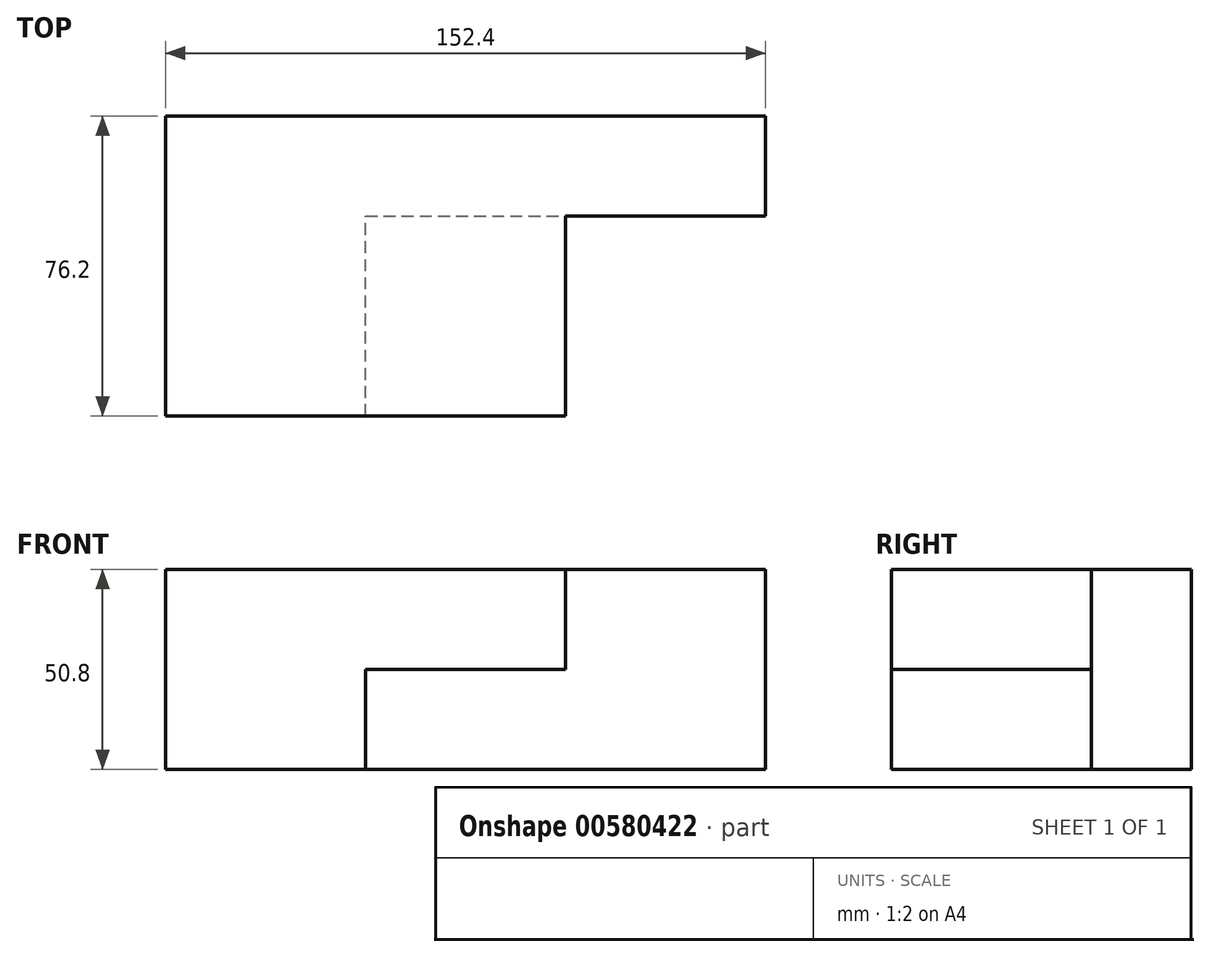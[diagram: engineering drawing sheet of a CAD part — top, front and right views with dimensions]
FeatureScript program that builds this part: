
annotation { "Feature Type Name" : "Feature", "Feature Type Description" : "" }
export const myFeature = defineFeature(function(context is Context, id is Id, definition is map)
    precondition{}
    {
        {
            var Q0;
            Q0=qCreatedBy(makeId("Front.planeOp"),FACE);
            var sketch = newSketch(context, id + "F0", { "sketchPlane" : qUnion([Q0])});
            skLineSegment(sketch, "E0.bottom", {"start": v(-55.37, 21.3) * mm, "end": v(97.03, 21.3) * mm});
            skLineSegment(sketch, "E0.top", {"start": v(-55.37, -29.5) * mm, "end": v(97.03, -29.5) * mm});
            skLineSegment(sketch, "E0.left", {"start": v(-55.37, 21.3) * mm, "end": v(-55.37, -29.5) * mm});
            skLineSegment(sketch, "E0.right", {"start": v(97.03, 21.3) * mm, "end": v(97.03, -29.5) * mm});
            skLineSegment(sketch, "E1", {"start": v(-4.57, -29.5) * mm, "end": v(-4.57, -4.1) * mm});
            skLineSegment(sketch, "E2", {"start": v(-4.57, -4.1) * mm, "end": v(46.23, -4.1) * mm});
            skLineSegment(sketch, "E3", {"start": v(46.23, -4.1) * mm, "end": v(46.23, 21.3) * mm});
            skSolve(sketch);
        }
        {
            var Q0;
            {var subQ0=sQuery(id+"F0.wireOp",EDGE,"E0.right");Q0=makeQuery(id+"F0.imprint","IMPRINT",FACE,{"disambiguationData":[TD([[makeQuery(id+"F0.imprint","IMPRINT",EDGE,{"derivedFrom":subQ0}),-1.0]])]});}
            extrude(context, id + "F1", {"entities" : qUnion([Q0]), "depth" : 25.4 * mm, "offsetDistance" : 25.4 * mm});
        }
        {
            var Q0;
            {var subQ1=sQuery(id+"F0.wireOp",EDGE,"E0.left");Q0=makeQuery(id+"F0.imprint","IMPRINT",FACE,{"disambiguationData":[TD([[makeQuery(id+"F0.imprint","IMPRINT",EDGE,{"derivedFrom":subQ1}),1.0]])]});}
            extrude(context, id + "F2", {"entities" : qUnion([Q0]), "operationType" : NewBodyOperationType.ADD, "depth" : 76.2 * mm, "offsetDistance" : 25.4 * mm});
        }
    });
